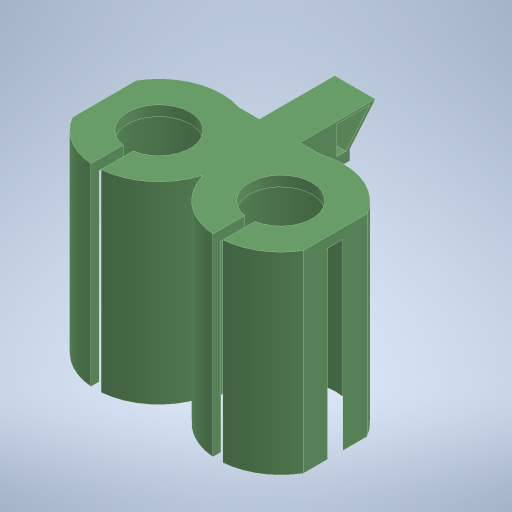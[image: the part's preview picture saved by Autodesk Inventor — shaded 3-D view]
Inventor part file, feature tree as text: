
AUTODESK INVENTOR PART (.ipt)
format: ipt  version: 2023.4 (Build 274418000, 418)  size: 410,112 bytes
history: native  units: in
note: dims shown in document units (in); Inventor stores cm internally (conversion verified against a paired STEP export)
features: sketch x9, extrude x7, other x3, hole x1
ambient origin geometry x8: Origin, YZ Plane, XZ Plane, XY Plane, X Axis, Y Axis, Z Axis, Center Point
bodies: Solid1 (feature_tree)
feature tree (20):
  other  "main_manifold_8v_v02.ipt"
  other  "vial_ST_01.ipt"
  other  "mainPlate.ipt"
  sketch  "Sketch:VH: vials"  dims[d319=0.3in d1=0.3937in]
  sketch  "Sketch:VH: side cutout"  dims[d5=0.615in d8=0.1in d9=0.0in]
  extrude  "Ex: top of vials"  TaperAngle=0.0deg  [1 undecoded]
  extrude  "Ex: around vials"  Depth=0.3937in
  extrude  "Ex: side cutout"  Depth=0.1in TaperAngle=0.0deg
  extrude  "Ex: screw area"  Depth=1.8in
  sketch  "Sketch:VH: screw hole"  dims[d10=1.8in d11=0.0in d12=0.536in]
  hole  "Hole: screw to MP"  [1 undecoded]
  sketch  "Sketch:VH: extend front"  dims[d13=0.0in d14=0.0in d15=0.4in]
  extrude  "Ex: front cutout"  Depth=0.3in TaperAngle=0.0deg
  extrude  "Ex: under MP"  TaperAngle=0.0deg  [1 undecoded]
  extrude  "Extrusion12"  Depth=0.1in
  sketch  "Sketch:MM: flow sensor"  dims[d18=0.3635in d19=0.3in d20=0.0in]
  sketch  "Sketch:VH: screw part"  dims[d21=0.173in]
  sketch  "Sketch:VH: front cutout"  dims[d22=0.75in d23=0.375in d24=0.25in d25=0.5635in d26=0.21in d27=0.0in]
  sketch  "Sketch: under MP"  dims[d42=0.0in d43=0.0in d44=0.1in d47=0.02in d57=0.15in d58=0.2137in d59=0.3937in d297=0.175in d72=0.125in d75=0.1in d76=0.0in d77=0.126in d78=0.3436in d79=0.0421in d82=0.037in d83=0.1in d84=0.0in d85=0.0213in d86=0.0283in d87=0.0172in d89=0.2599in d90=0.2787in d91=0.089in d60=0.0344in d61=0.5in d62=0.0344in]
  sketch  "Sketch12"  dims[d0=0.3937in d439=0.0in]
note: 3 required parameter values undecoded (feature->parameter linkage not recoverable at this tier; creation-order binding heuristic only, values carry confidence <= 0.55)
